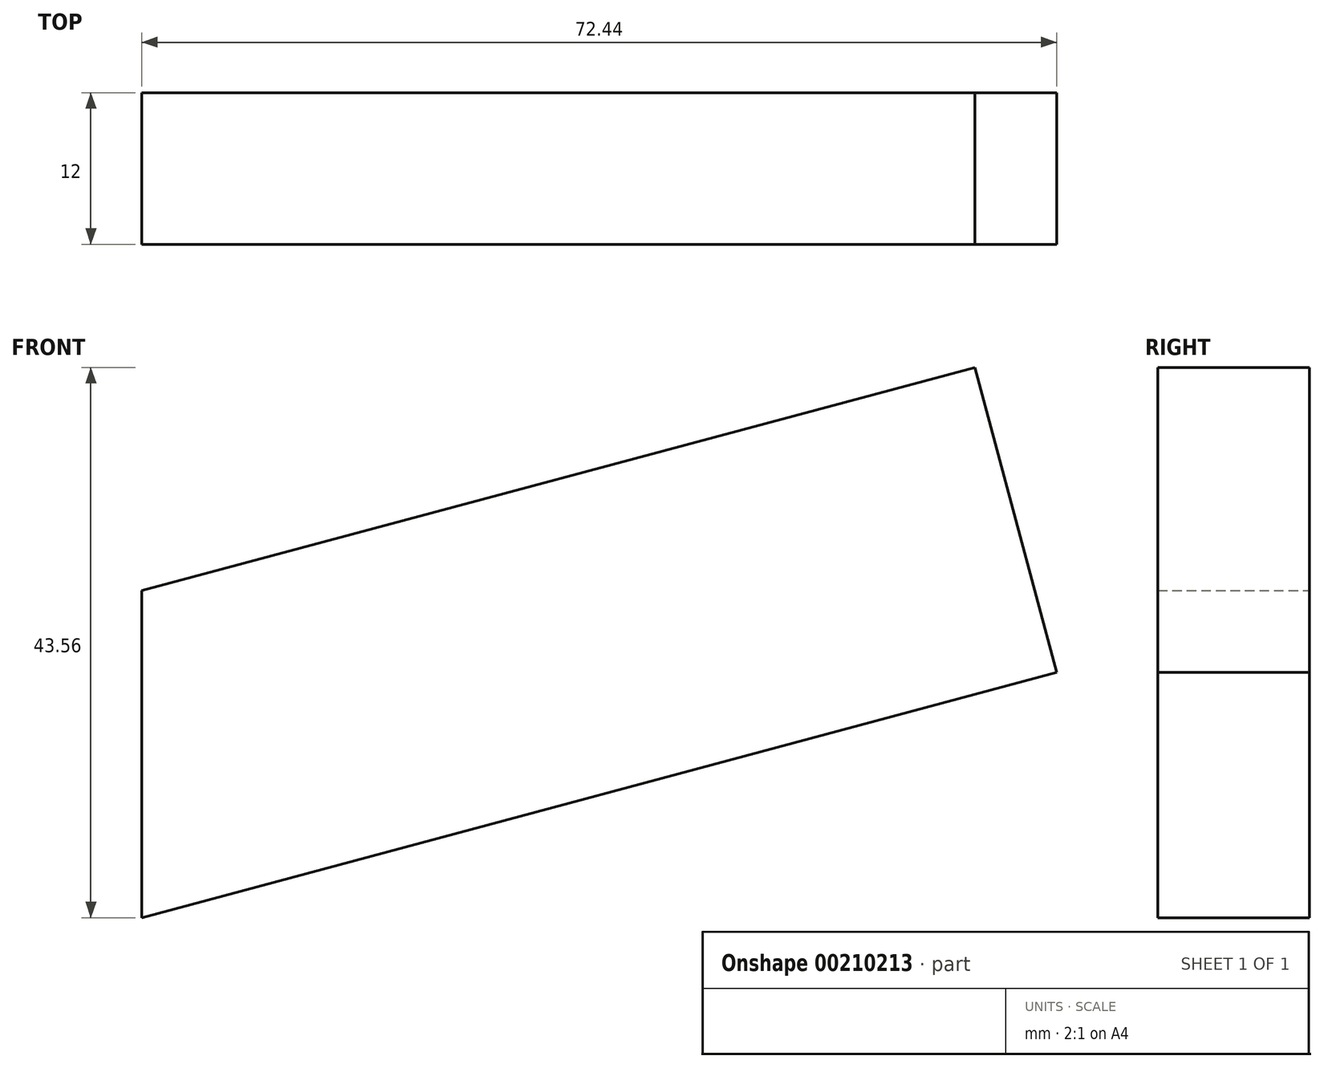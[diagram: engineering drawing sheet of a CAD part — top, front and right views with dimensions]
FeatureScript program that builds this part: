
annotation { "Feature Type Name" : "Feature", "Feature Type Description" : "" }
export const myFeature = defineFeature(function(context is Context, id is Id, definition is map)
    precondition{}
    {
        {
            var Q0;
            Q0=qCreatedBy(makeId("Front.planeOp"),FACE);
            var sketch = newSketch(context, id + "F0", { "sketchPlane" : qUnion([Q0])});
            skLineSegment(sketch, "E0", {"start": v(0, 0) * mm, "end": v(72.44, 19.41) * mm});
            skLineSegment(sketch, "E1", {"start": v(72.44, 19.41) * mm, "end": v(65.97, 43.56) * mm});
            skLineSegment(sketch, "E2", {"start": v(65.97, 43.56) * mm, "end": v(0, 25.88) * mm});
            skLineSegment(sketch, "E3", {"start": v(0, 25.88) * mm, "end": v(0, 0) * mm});
            skSolve(sketch);
        }
        {
            var Q0;
            Q0 = qSketchRegion(id + "F0", true);
            extrude(context, id + "F1", {"entities" : qUnion([Q0]), "depth" : 12 * mm});
        }
    });
